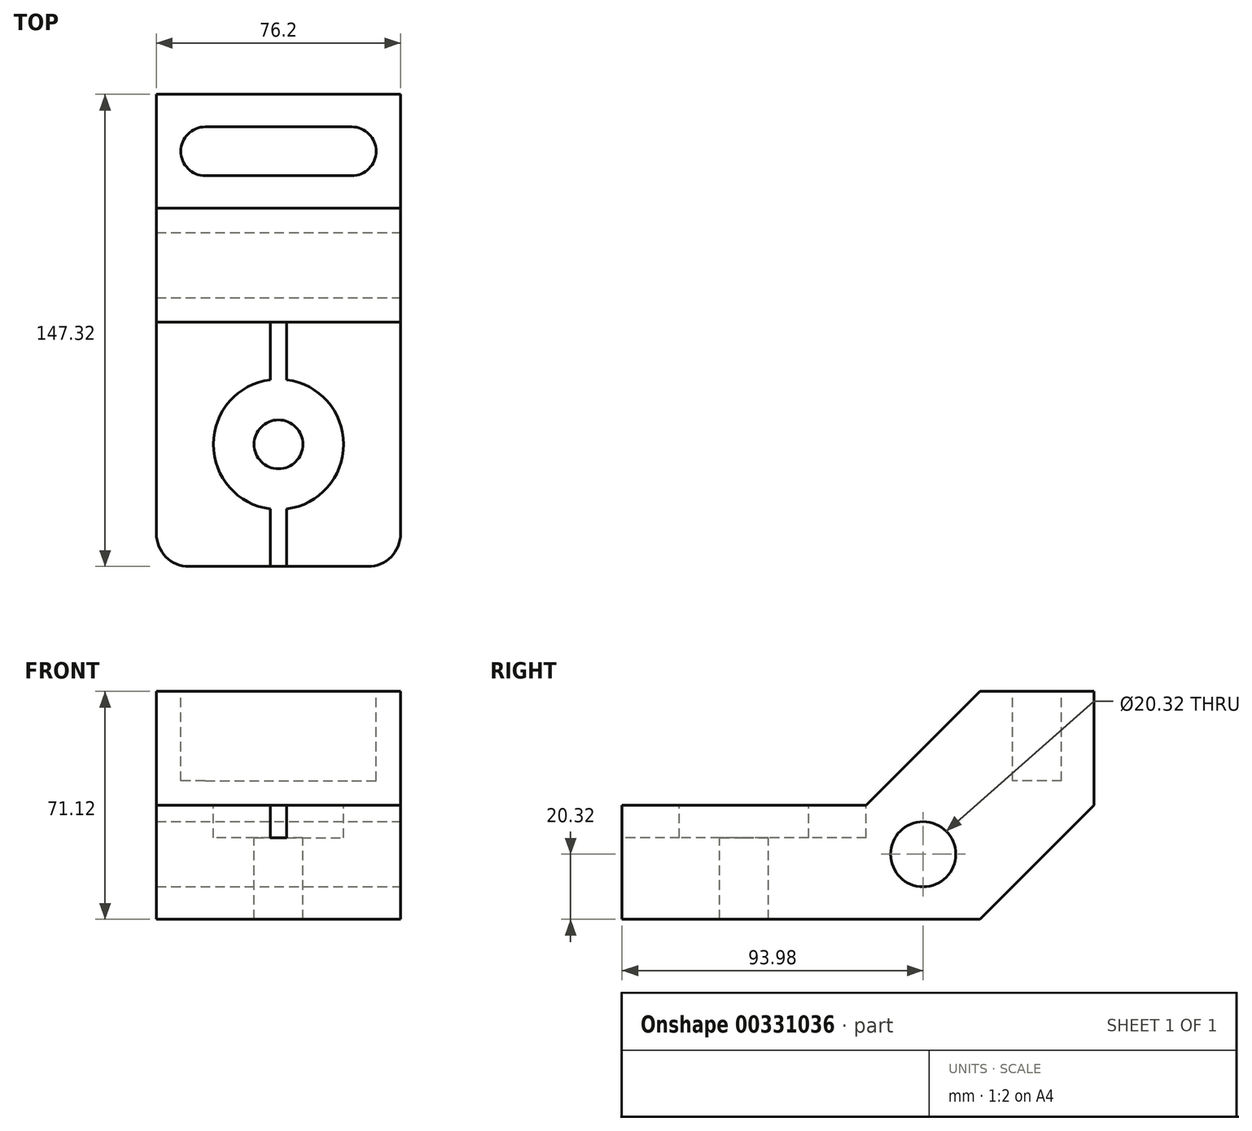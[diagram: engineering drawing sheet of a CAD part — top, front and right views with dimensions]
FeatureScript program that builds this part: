
annotation { "Feature Type Name" : "Feature", "Feature Type Description" : "" }
export const myFeature = defineFeature(function(context is Context, id is Id, definition is map)
    precondition{}
    {
        {
            var Q0;
            Q0=qCreatedBy(makeId("Right.planeOp"),FACE);
            var sketch = newSketch(context, id + "F0", { "sketchPlane" : qUnion([Q0])});
            skLineSegment(sketch, "E0", {"start": v(0, 0) * mm, "end": v(111.76, 0) * mm});
            skLineSegment(sketch, "E1", {"start": v(111.76, 0) * mm, "end": v(147.32, 0) * mm, "construction": true});
            skLineSegment(sketch, "E2", {"start": v(147.32, 0) * mm, "end": v(147.32, 35.56) * mm, "construction": true});
            skLineSegment(sketch, "E3", {"start": v(111.76, 0) * mm, "end": v(147.32, 35.56) * mm});
            skLineSegment(sketch, "E4", {"start": v(147.32, 35.56) * mm, "end": v(147.32, 71.12) * mm});
            skLineSegment(sketch, "E5", {"start": v(147.32, 71.12) * mm, "end": v(111.76, 71.12) * mm});
            skLineSegment(sketch, "E6", {"start": v(0, 0) * mm, "end": v(0, 35.56) * mm});
            skLineSegment(sketch, "E7", {"start": v(0, 35.56) * mm, "end": v(76.2, 35.56) * mm});
            skLineSegment(sketch, "E8", {"start": v(76.2, 35.56) * mm, "end": v(111.76, 71.12) * mm});
            skSolve(sketch);
        }
        {
            var Q0;
            Q0=makeQuery(id+"F0.imprint","IMPRINT",FACE,{"disambiguationData":[TD([[makeQuery(id+"F0.imprint","IMPRINT",EDGE,{"derivedFrom":sQuery(id+"F0.wireOp",EDGE,"E0")}),1.0]])]});
            extrude(context, id + "F1", {"entities" : qUnion([Q0]), "endBound" : BoundingType.SYMMETRIC, "depth" : 76.2 * mm});
        }
        {
            var Q0;
            Q0=makeQuery(id+"F1.opExtrude","SWEPT_FACE",FACE,{"disambiguationData":[OSD([sQuery(id+"F0.wireOp",EDGE,"E7")])]});
            var sketch = newSketch(context, id + "F2", { "sketchPlane" : qUnion([Q0])});
            skPoint(sketch, "E9", {"position": v(0, 38.1) * mm});
            skPoint(sketch, "E9.positionSnap0", {"position": v(-38.1, 38.1) * mm});
            skSolve(sketch);
        }
        {
            var Q0;
            Q0=sQuery(id+"F2.wireOp",VERTEX,"E9");
            var Q1;
            Q1=makeQuery(id+"F1.opExtrude","SWEPT_BODY",BODY,{"disambiguationData":[OSD([sQuery(id+"F0.wireOp",EDGE,"E0"),sQuery(id+"F0.wireOp",EDGE,"E3"),sQuery(id+"F0.wireOp",EDGE,"E4"),sQuery(id+"F0.wireOp",EDGE,"E5"),sQuery(id+"F0.wireOp",EDGE,"E6"),sQuery(id+"F0.wireOp",EDGE,"E7"),sQuery(id+"F0.wireOp",EDGE,"E8")])]});
            hole(context, id + "F3", {"style" : HoleStyle.C_BORE, "endStyle" : HoleEndStyle.THROUGH, "holeDiameter" : 15.24 * mm, "cBoreDiameter" : 40.64 * mm, "cBoreDepth" : 10.16 * mm, "tappedDepth" : 12.7 * mm, "tapClearance" : 3, "locations" : qUnion([Q0]), "scope" : qUnion([Q1])});
        }
        {
            var Q0;
            Q0=makeQuery(id+"F1.opExtrude","SWEPT_FACE",FACE,{"disambiguationData":[OSD([sQuery(id+"F0.wireOp",EDGE,"E6")])]});
            var sketch = newSketch(context, id + "F4", { "sketchPlane" : qUnion([Q0])});
            skLineSegment(sketch, "E10", {"start": v(0, 35.56) * mm, "end": v(-2.54, 35.56) * mm});
            skLineSegment(sketch, "E11", {"start": v(-2.54, 35.56) * mm, "end": v(-2.54, 25.4) * mm});
            skLineSegment(sketch, "E12", {"start": v(-2.54, 25.4) * mm, "end": v(2.54, 25.4) * mm});
            skLineSegment(sketch, "E13", {"start": v(2.54, 25.4) * mm, "end": v(2.54, 35.56) * mm});
            skLineSegment(sketch, "E14", {"start": v(2.54, 35.56) * mm, "end": v(0, 35.56) * mm});
            skSolve(sketch);
        }
        {
            var Q0;
            Q0=makeQuery(id+"F4.imprint","IMPRINT",FACE,{"disambiguationData":[TD([[makeQuery(id+"F4.imprint","IMPRINT",EDGE,{"derivedFrom":sQuery(id+"F4.wireOp",EDGE,"E10")}),1.0]])]});
            extrude(context, id + "F5", {"entities" : qUnion([Q0]), "operationType" : NewBodyOperationType.REMOVE, "oppositeDirection" : true, "depth" : 76.2 * mm});
        }
        {
            var Q0;
            Q0=makeQuery(id+"F1.opExtrude","CAP_FACE",FACE,{"disambiguationData":[OSD([sQuery(id+"F0.wireOp",EDGE,"E0"),sQuery(id+"F0.wireOp",EDGE,"E3"),sQuery(id+"F0.wireOp",EDGE,"E4"),sQuery(id+"F0.wireOp",EDGE,"E5"),sQuery(id+"F0.wireOp",EDGE,"E6"),sQuery(id+"F0.wireOp",EDGE,"E7"),sQuery(id+"F0.wireOp",EDGE,"E8")])],"isStart":false});
            var sketch = newSketch(context, id + "F6", { "sketchPlane" : qUnion([Q0])});
            skLineSegment(sketch, "E15.0.0", {"start": v(111.76, 71.12) * mm, "end": v(76.2, 35.56) * mm});
            skLineSegment(sketch, "E15.0.1", {"start": v(76.2, 35.56) * mm, "end": v(0, 35.56) * mm});
            skLineSegment(sketch, "E15.0.2", {"start": v(0, 35.56) * mm, "end": v(0, 0) * mm});
            skLineSegment(sketch, "E15.0.3", {"start": v(0, 0) * mm, "end": v(111.76, 0) * mm});
            skLineSegment(sketch, "E15.0.4", {"start": v(111.76, 0) * mm, "end": v(147.32, 35.56) * mm});
            skLineSegment(sketch, "E15.0.5", {"start": v(147.32, 35.56) * mm, "end": v(147.32, 71.12) * mm});
            skLineSegment(sketch, "E15.0.6", {"start": v(147.32, 71.12) * mm, "end": v(111.76, 71.12) * mm});
            skCircle(sketch, "E16", {"center": v(93.98, 20.32) * mm, "radius": 10.16 * mm});
            skSolve(sketch);
        }
        {
            var Q0;
            Q0=makeQuery(id+"F6.imprint","IMPRINT",FACE,{"disambiguationData":[TD([[makeQuery(id+"F6.imprint","IMPRINT",EDGE,{"derivedFrom":sQuery(id+"F6.wireOp",EDGE,"E16")}),1.0]])]});
            extrude(context, id + "F7", {"entities" : qUnion([Q0]), "operationType" : NewBodyOperationType.REMOVE, "oppositeDirection" : true, "depth" : 76.2 * mm});
        }
        {
            var Q0;
            Q0=makeQuery(id+"F1.opExtrude","SWEPT_FACE",FACE,{"disambiguationData":[OSD([sQuery(id+"F0.wireOp",EDGE,"E5")])]});
            var sketch = newSketch(context, id + "F8", { "sketchPlane" : qUnion([Q0])});
            skLineSegment(sketch, "E17.0.0", {"start": v(-38.1, 147.32) * mm, "end": v(-38.1, 111.76) * mm});
            skLineSegment(sketch, "E17.0.1", {"start": v(-38.1, 111.76) * mm, "end": v(38.1, 111.76) * mm});
            skLineSegment(sketch, "E17.0.2", {"start": v(38.1, 111.76) * mm, "end": v(38.1, 147.32) * mm});
            skLineSegment(sketch, "E17.0.3", {"start": v(38.1, 147.32) * mm, "end": v(-38.1, 147.32) * mm});
            skArc(sketch, "E18", {"start": v(-22.86, 137.16) * mm, "mid": v(-30.48, 129.54) * mm, "end": v(-22.86, 121.92) * mm});
            skArc(sketch, "E19", {"start": v(22.86, 121.92) * mm, "mid": v(30.48, 129.54) * mm, "end": v(22.86, 137.16) * mm});
            skLineSegment(sketch, "E20", {"start": v(-22.86, 137.16) * mm, "end": v(22.86, 137.16) * mm});
            skLineSegment(sketch, "E21", {"start": v(22.86, 121.92) * mm, "end": v(-22.86, 121.92) * mm});
            skSolve(sketch);
        }
        {
            var Q0;
            Q0=makeQuery(id+"F8.imprint","IMPRINT",FACE,{"disambiguationData":[TD([[makeQuery(id+"F8.imprint","IMPRINT",EDGE,{"derivedFrom":sQuery(id+"F8.wireOp",EDGE,"E18")}),1.0]])]});
            extrude(context, id + "F9", {"entities" : qUnion([Q0]), "operationType" : NewBodyOperationType.REMOVE, "oppositeDirection" : true, "depth" : 27.94 * mm});
        }
        {
            var Q0;
            Q0=makeQuery(id+"F1.opExtrude","CAP_EDGE",EDGE,{"disambiguationData":[OSD([sQuery(id+"F0.wireOp",EDGE,"E6")])],"isStart":false});
            var Q1;
            Q1=makeQuery(id+"F1.opExtrude","CAP_EDGE",EDGE,{"disambiguationData":[OSD([sQuery(id+"F0.wireOp",EDGE,"E6")])],"isStart":true});
            fillet(context, id + "F10", {"entities" : qUnion([Q0, Q1]), "radius" : 10.16 * mm, "tangentPropagation" : true, "allowEdgeOverflow" : false});
        }
    });
